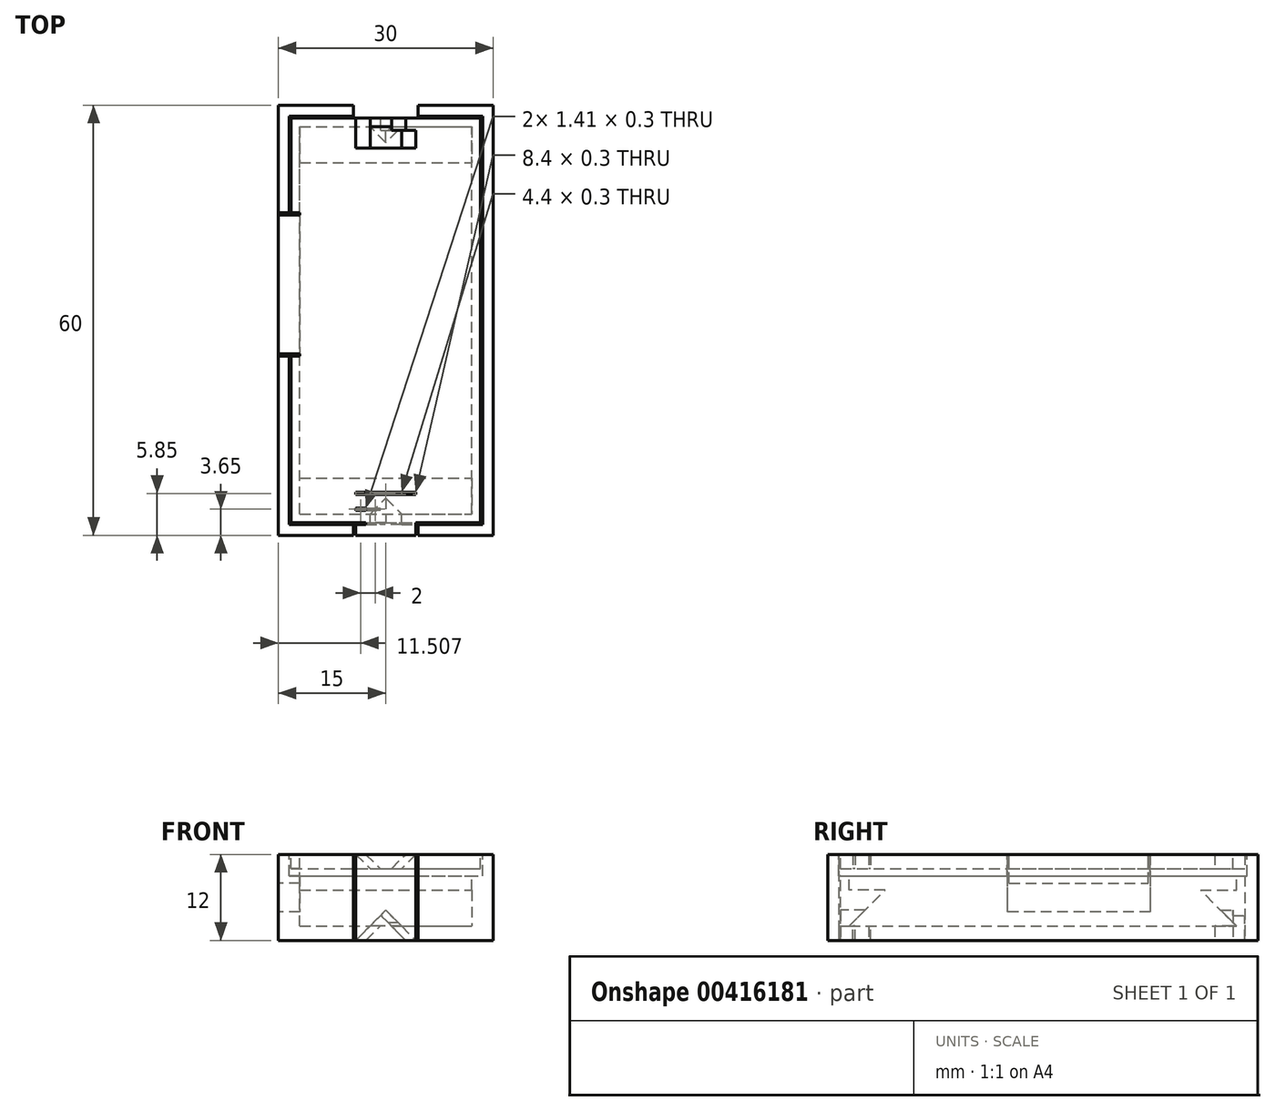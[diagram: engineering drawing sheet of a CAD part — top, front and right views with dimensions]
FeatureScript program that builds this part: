
annotation { "Feature Type Name" : "Feature", "Feature Type Description" : "" }
export const myFeature = defineFeature(function(context is Context, id is Id, definition is map)
    precondition{}
    {
        {
            var Q0;
            Q0=qCreatedBy(makeId("Top.planeOp"),FACE);
            var sketch = newSketch(context, id + "F0", { "sketchPlane" : qUnion([Q0])});
            skLineSegment(sketch, "E0.bottom", {"start": v(0, 0) * mm, "end": v(30, 0) * mm});
            skLineSegment(sketch, "E0.top", {"start": v(0, 60) * mm, "end": v(30, 60) * mm});
            skLineSegment(sketch, "E0.left", {"start": v(0, 0) * mm, "end": v(0, 60) * mm});
            skLineSegment(sketch, "E0.right", {"start": v(30, 0) * mm, "end": v(30, 60) * mm});
            skLineSegment(sketch, "E1.0", {"start": v(1.5, 1.5) * mm, "end": v(1.5, 58.5) * mm});
            skLineSegment(sketch, "E1.1", {"start": v(1.5, 1.5) * mm, "end": v(28.5, 1.5) * mm});
            skLineSegment(sketch, "E1.2", {"start": v(28.5, 1.5) * mm, "end": v(28.5, 58.5) * mm});
            skLineSegment(sketch, "E1.3", {"start": v(1.5, 58.5) * mm, "end": v(28.5, 58.5) * mm});
            skLineSegment(sketch, "E2.0", {"start": v(1.8, 1.8) * mm, "end": v(1.8, 58.2) * mm});
            skLineSegment(sketch, "E2.1", {"start": v(1.8, 1.8) * mm, "end": v(28.2, 1.8) * mm});
            skLineSegment(sketch, "E2.2", {"start": v(28.2, 1.8) * mm, "end": v(28.2, 58.2) * mm});
            skLineSegment(sketch, "E2.3", {"start": v(1.8, 58.2) * mm, "end": v(28.2, 58.2) * mm});
            skLineSegment(sketch, "E3.0", {"start": v(3, 3) * mm, "end": v(3, 57) * mm});
            skLineSegment(sketch, "E3.1", {"start": v(3, 3) * mm, "end": v(27, 3) * mm});
            skLineSegment(sketch, "E3.2", {"start": v(27, 3) * mm, "end": v(27, 57) * mm});
            skLineSegment(sketch, "E3.3", {"start": v(3, 57) * mm, "end": v(27, 57) * mm});
            skSolve(sketch);
        }
        {
            var Q0;
            Q0=makeQuery(id+"F0.imprint","IMPRINT",FACE,{"disambiguationData":[TD([[makeQuery(id+"F0.imprint","IMPRINT",EDGE,{"derivedFrom":sQuery(id+"F0.wireOp",EDGE,"E0.bottom")}),1.0]])]});
            var Q1;
            Q1=makeQuery(id+"F0.imprint","IMPRINT",FACE,{"disambiguationData":[TD([[makeQuery(id+"F0.imprint","IMPRINT",EDGE,{"derivedFrom":sQuery(id+"F0.wireOp",EDGE,"E1.0")}),-1.0]])]});
            var Q2;
            Q2=makeQuery(id+"F0.imprint","IMPRINT",FACE,{"disambiguationData":[TD([[makeQuery(id+"F0.imprint","IMPRINT",EDGE,{"derivedFrom":sQuery(id+"F0.wireOp",EDGE,"E2.0")}),-1.0]])]});
            extrude(context, id + "F1", {"entities" : qUnion([Q0, Q1, Q2]), "oppositeDirection" : true, "depth" : 10 * mm, "offsetDistance" : 25 * mm});
        }
        {
            var Q0;
            Q0=makeQuery(id+"F0.imprint","IMPRINT",FACE,{"disambiguationData":[TD([[makeQuery(id+"F0.imprint","IMPRINT",EDGE,{"derivedFrom":sQuery(id+"F0.wireOp",EDGE,"E2.0")}),-1.0]])]});
            var Q1;
            Q1=makeQuery(id+"F0.imprint","IMPRINT",FACE,{"disambiguationData":[TD([[makeQuery(id+"F0.imprint","IMPRINT",EDGE,{"derivedFrom":sQuery(id+"F0.wireOp",EDGE,"E1.0")}),-1.0]])]});
            extrude(context, id + "F2", {"entities" : qUnion([Q0, Q1]), "operationType" : NewBodyOperationType.REMOVE, "oppositeDirection" : true, "depth" : 3 * mm, "offsetDistance" : 25 * mm});
        }
        {
            var Q0;
            Q0=makeQuery(id+"F1.opExtrude","CAP_FACE",FACE,{"disambiguationData":[OSD([sQuery(id+"F0.wireOp",EDGE,"E0.bottom"),sQuery(id+"F0.wireOp",EDGE,"E0.top"),sQuery(id+"F0.wireOp",EDGE,"E0.left"),sQuery(id+"F0.wireOp",EDGE,"E0.right"),sQuery(id+"F0.wireOp",EDGE,"E3.0"),sQuery(id+"F0.wireOp",EDGE,"E3.1"),sQuery(id+"F0.wireOp",EDGE,"E3.2"),sQuery(id+"F0.wireOp",EDGE,"E3.3")])],"isStart":false});
            var sketch = newSketch(context, id + "F3", { "sketchPlane" : qUnion([Q0])});
            skLineSegment(sketch, "E4.0", {"start": v(0, 0) * mm, "end": v(30, 0) * mm});
            skLineSegment(sketch, "E5.0", {"start": v(30, 0) * mm, "end": v(30, -60) * mm});
            skLineSegment(sketch, "E6.0", {"start": v(0, 0) * mm, "end": v(0, -60) * mm});
            skLineSegment(sketch, "E7.0", {"start": v(0, -60) * mm, "end": v(30, -60) * mm});
            skSolve(sketch);
        }
        {
            var Q0;
            Q0 = qSketchRegion(id + "F3", true);
            extrude(context, id + "F4", {"entities" : qUnion([Q0]), "operationType" : NewBodyOperationType.ADD, "depth" : 2 * mm, "offsetDistance" : 25 * mm});
        }
        {
            var Q0;
            Q0=makeQuery(id+"F1.opExtrude","SWEPT_FACE",FACE,{"disambiguationData":[OSD([sQuery(id+"F0.wireOp",EDGE,"E3.2")])]});
            var sketch = newSketch(context, id + "F5", { "sketchPlane" : qUnion([Q0])});
            skLineSegment(sketch, "E8", {"start": v(-3, -10) * mm, "end": v(-3, -5) * mm});
            skLineSegment(sketch, "E9", {"start": v(-3, -5) * mm, "end": v(-8, -5) * mm});
            skLineSegment(sketch, "E10", {"start": v(-8, -5) * mm, "end": v(-3, -10) * mm});
            skLineSegment(sketch, "E11", {"start": v(-57, -10) * mm, "end": v(-57, -5) * mm});
            skPoint(sketch, "E11.endSnap0", {"position": v(-5.5, -5) * mm});
            skLineSegment(sketch, "E12", {"start": v(-57, -5) * mm, "end": v(-52, -5) * mm});
            skLineSegment(sketch, "E13", {"start": v(-52, -5) * mm, "end": v(-57, -10) * mm});
            skSolve(sketch);
        }
        {
            var Q0;
            Q0 = qSketchRegion(id + "F5", true);
            var Q1;
            Q1=makeQuery(id+"F1.opExtrude","SWEPT_FACE",FACE,{"disambiguationData":[OSD([sQuery(id+"F0.wireOp",EDGE,"E3.0")])]});
            extrude(context, id + "F6", {"entities" : qUnion([Q0]), "operationType" : NewBodyOperationType.ADD, "endBound" : BoundingType.UP_TO_SURFACE, "depth" : 25 * mm, "endBoundEntityFace" : qUnion([Q1]), "offsetDistance" : 25 * mm});
        }
        {
            var Q0;
            Q0=makeQuery(id+"F0.imprint","IMPRINT",FACE,{"disambiguationData":[TD([[makeQuery(id+"F0.imprint","IMPRINT",EDGE,{"derivedFrom":sQuery(id+"F0.wireOp",EDGE,"E2.0")}),-1.0]])]});
            var Q1;
            Q1=makeQuery(id+"F0.imprint","IMPRINT",FACE,{"disambiguationData":[TD([[makeQuery(id+"F0.imprint","IMPRINT",EDGE,{"derivedFrom":sQuery(id+"F0.wireOp",EDGE,"E3.0")}),-1.0]])]});
            extrude(context, id + "F7", {"entities" : qUnion([Q0, Q1]), "oppositeDirection" : true, "depth" : 2 * mm, "offsetDistance" : 25 * mm});
        }
        {
            var Q0;
            Q0=makeQuery(id+"F7.opExtrude","CAP_EDGE",EDGE,{"disambiguationData":[OSD([sQuery(id+"F0.wireOp",EDGE,"E2.1")])],"isStart":false});
            cPlane(context, id + "F8", {"entities" : qUnion([Q0]), "cplaneType" : CPlaneType.MID_PLANE, "offset" : 25 * mm, "width" : 150 * mm, "height" : 150 * mm});
        }
        {
            var Q0;
            Q0=makeQuery(id+"F4.boolean.opBoolean","MERGE",FACE,{"derivedFrom":[makeQuery(id+"F1.opExtrude","SWEPT_FACE",FACE,{"disambiguationData":[OSD([sQuery(id+"F0.wireOp",EDGE,"E0.bottom")])]}),makeQuery(id+"F4.opExtrude","SWEPT_FACE",FACE,{"disambiguationData":[OSD([sQuery(id+"F3.wireOp",EDGE,"E4.0")])]})]});
            var sketch = newSketch(context, id + "F9", { "sketchPlane" : qUnion([Q0])});
            skLineSegment(sketch, "E14", {"start": v(10.5, 0) * mm, "end": v(10.5, -12) * mm});
            skLineSegment(sketch, "E15", {"start": v(19.5, 0) * mm, "end": v(19.5, -12) * mm});
            skLineSegment(sketch, "E16", {"start": v(10.8, 0) * mm, "end": v(12.8, -2) * mm});
            skLineSegment(sketch, "E17", {"start": v(19.2, 0) * mm, "end": v(17.2, -2) * mm});
            skLineSegment(sketch, "E18", {"start": v(12.21, 0) * mm, "end": v(14.21, -2) * mm});
            skLineSegment(sketch, "E19", {"start": v(12.8, -2) * mm, "end": v(17.2, -2) * mm});
            skLineSegment(sketch, "E20", {"start": v(10.8, 0) * mm, "end": v(19.2, 0) * mm});
            skLineSegment(sketch, "E21", {"start": v(10.8, 0) * mm, "end": v(10.8, -12) * mm, "construction": true});
            skLineSegment(sketch, "E22", {"start": v(19.2, 0) * mm, "end": v(19.2, -12) * mm, "construction": true});
            skLineSegment(sketch, "E23", {"start": v(10.8, -12) * mm, "end": v(15, -7.8) * mm});
            skLineSegment(sketch, "E24", {"start": v(15, -7.8) * mm, "end": v(19.2, -12) * mm});
            skLineSegment(sketch, "E25", {"start": v(12.21, -12) * mm, "end": v(15.7, -8.5) * mm});
            skSolve(sketch);
        }
        {
            var Q0;
            {var subQ0=sQuery(id+"F9.wireOp",EDGE,"E14");Q0=makeQuery(id+"F9.imprint","IMPRINT",FACE,{"disambiguationData":[TD([[makeQuery(id+"F9.imprint","IMPRINT",EDGE,{"derivedFrom":subQ0}),1.0]])]});}
            var Q1;
            {var subQ0=sQuery(id+"F9.wireOp",EDGE,"E16");Q1=makeQuery(id+"F9.imprint","IMPRINT",FACE,{"disambiguationData":[TD([[makeQuery(id+"F9.imprint","IMPRINT",EDGE,{"derivedFrom":subQ0}),1.0]])]});}
            var Q2;
            {var subQ0=sQuery(id+"F9.wireOp",EDGE,"E18");Q2=makeQuery(id+"F9.imprint","IMPRINT",FACE,{"disambiguationData":[TD([[makeQuery(id+"F9.imprint","IMPRINT",EDGE,{"derivedFrom":subQ0}),1.0]])]});}
            var Q3;
            {var subQ0=sQuery(id+"F9.wireOp",EDGE,"E17");Q3=makeQuery(id+"F9.imprint","IMPRINT",FACE,{"disambiguationData":[TD([[makeQuery(id+"F9.imprint","IMPRINT",EDGE,{"derivedFrom":subQ0}),-1.0]])]});}
            var Q4;
            {var subQ0=sQuery(id+"F9.wireOp",EDGE,"E25");Q4=makeQuery(id+"F9.imprint","IMPRINT",FACE,{"disambiguationData":[TD([[makeQuery(id+"F9.imprint","IMPRINT",EDGE,{"derivedFrom":subQ0}),-1.0]])]});}
            var Q5;
            {var subQ0=sQuery(id+"F9.wireOp",EDGE,"E23");Q5=makeQuery(id+"F9.imprint","IMPRINT",FACE,{"disambiguationData":[TD([[makeQuery(id+"F9.imprint","IMPRINT",EDGE,{"derivedFrom":subQ0}),-1.0]])]});}
            var Q6;
            Q6=makeQuery(id+"F7.opExtrude","SWEPT_FACE",FACE,{"disambiguationData":[OSD([sQuery(id+"F0.wireOp",EDGE,"E2.1")])]});
            extrude(context, id + "F10", {"entities" : qUnion([Q0, Q1, Q2, Q3, Q4, Q5]), "operationType" : NewBodyOperationType.REMOVE, "endBound" : BoundingType.UP_TO_SURFACE, "oppositeDirection" : true, "depth" : 1.5 * mm, "endBoundEntityFace" : qUnion([Q6]), "offsetDistance" : 25 * mm});
        }
        {
            var Q0;
            {var subQ0=sQuery(id+"F9.wireOp",EDGE,"E18");Q0=makeQuery(id+"F9.imprint","IMPRINT",FACE,{"disambiguationData":[TD([[makeQuery(id+"F9.imprint","IMPRINT",EDGE,{"derivedFrom":subQ0}),1.0]])]});}
            extrude(context, id + "F11", {"entities" : qUnion([Q0]), "operationType" : NewBodyOperationType.REMOVE, "oppositeDirection" : true, "depth" : 6 * mm, "offsetDistance" : 25 * mm});
        }
        {
            var Q0;
            {var subQ0=sQuery(id+"F9.wireOp",EDGE,"E16");Q0=makeQuery(id+"F9.imprint","IMPRINT",FACE,{"disambiguationData":[TD([[makeQuery(id+"F9.imprint","IMPRINT",EDGE,{"derivedFrom":subQ0}),1.0]])]});}
            extrude(context, id + "F12", {"entities" : qUnion([Q0]), "operationType" : NewBodyOperationType.REMOVE, "oppositeDirection" : true, "depth" : 6 * mm, "offsetDistance" : 25 * mm, "hasSecondDirection" : true, "secondDirectionOppositeDirection" : true, "secondDirectionDepth" : 3.5 * mm});
        }
        {
            var Q0;
            Q0=makeQuery(id+"F4.boolean.opBoolean","MERGE",FACE,{"derivedFrom":[makeQuery(id+"F1.opExtrude","SWEPT_FACE",FACE,{"disambiguationData":[OSD([sQuery(id+"F0.wireOp",EDGE,"E0.top")])]}),makeQuery(id+"F4.opExtrude","SWEPT_FACE",FACE,{"disambiguationData":[OSD([sQuery(id+"F3.wireOp",EDGE,"E7.0")])]})]});
            var sketch = newSketch(context, id + "F13", { "sketchPlane" : qUnion([Q0])});
            skLineSegment(sketch, "E26.0", {"start": v(-19.5, 0) * mm, "end": v(-19.5, -12) * mm});
            skLineSegment(sketch, "E27.0", {"start": v(-10.5, 0) * mm, "end": v(-10.5, -12) * mm});
            skLineSegment(sketch, "E28.0", {"start": v(-10.8, 0) * mm, "end": v(-12.8, -2) * mm});
            skLineSegment(sketch, "E29.0", {"start": v(-10.8, 0) * mm, "end": v(-19.2, 0) * mm});
            skLineSegment(sketch, "E30.0", {"start": v(-12.8, -2) * mm, "end": v(-17.2, -2) * mm});
            skLineSegment(sketch, "E31.0", {"start": v(-19.2, 0) * mm, "end": v(-17.2, -2) * mm});
            skLineSegment(sketch, "E32", {"start": v(-15.79, -2) * mm, "end": v(-17.79, 0) * mm});
            skLineSegment(sketch, "E33.0", {"start": v(-10.8, -12) * mm, "end": v(-15, -7.8) * mm});
            skLineSegment(sketch, "E33.1", {"start": v(-15, -7.8) * mm, "end": v(-19.2, -12) * mm});
            skLineSegment(sketch, "E34", {"start": v(-14.3, -8.5) * mm, "end": v(-17.79, -12) * mm});
            skSolve(sketch);
        }
        {
            var Q0;
            {var subQ1=sQuery(id+"F13.wireOp",EDGE,"E26.0");Q0=makeQuery(id+"F13.imprint","IMPRINT",FACE,{"disambiguationData":[TD([[makeQuery(id+"F13.imprint","IMPRINT",EDGE,{"derivedFrom":subQ1}),1.0]])]});}
            var Q1;
            {var subQ0=sQuery(id+"F13.wireOp",EDGE,"E31.0");Q1=makeQuery(id+"F13.imprint","IMPRINT",FACE,{"disambiguationData":[TD([[makeQuery(id+"F13.imprint","IMPRINT",EDGE,{"derivedFrom":subQ0}),1.0]])]});}
            var Q2;
            {var subQ0=sQuery(id+"F13.wireOp",EDGE,"E28.0");Q2=makeQuery(id+"F13.imprint","IMPRINT",FACE,{"disambiguationData":[TD([[makeQuery(id+"F13.imprint","IMPRINT",EDGE,{"derivedFrom":subQ0}),-1.0]])]});}
            var Q3;
            {var subQ3=sQuery(id+"F13.wireOp",EDGE,"E34");Q3=makeQuery(id+"F13.imprint","IMPRINT",FACE,{"disambiguationData":[TD([[makeQuery(id+"F13.imprint","IMPRINT",EDGE,{"derivedFrom":subQ3}),1.0]])]});}
            var Q4;
            {var subQ0=sQuery(id+"F13.wireOp",EDGE,"E33.1");Q4=makeQuery(id+"F13.imprint","IMPRINT",FACE,{"disambiguationData":[TD([[makeQuery(id+"F13.imprint","IMPRINT",EDGE,{"derivedFrom":subQ0}),1.0]])]});}
            var Q5;
            Q5=makeQuery(id+"F7.opExtrude","SWEPT_FACE",FACE,{"disambiguationData":[OSD([sQuery(id+"F0.wireOp",EDGE,"E2.3")])]});
            extrude(context, id + "F14", {"entities" : qUnion([Q0, Q1, Q2, Q3, Q4]), "operationType" : NewBodyOperationType.REMOVE, "endBound" : BoundingType.UP_TO_SURFACE, "oppositeDirection" : true, "depth" : 1.3 * mm, "endBoundEntityFace" : qUnion([Q5]), "offsetDistance" : 25 * mm});
        }
        {
            var Q0;
            {var subQ0=sQuery(id+"F13.wireOp",EDGE,"E28.0");Q0=makeQuery(id+"F13.imprint","IMPRINT",FACE,{"disambiguationData":[TD([[makeQuery(id+"F13.imprint","IMPRINT",EDGE,{"derivedFrom":subQ0}),-1.0]])]});}
            extrude(context, id + "F15", {"entities" : qUnion([Q0]), "operationType" : NewBodyOperationType.REMOVE, "oppositeDirection" : true, "depth" : 6 * mm, "offsetDistance" : 25 * mm});
        }
        {
            var Q0;
            {var subQ0=sQuery(id+"F13.wireOp",EDGE,"E31.0");Q0=makeQuery(id+"F13.imprint","IMPRINT",FACE,{"disambiguationData":[TD([[makeQuery(id+"F13.imprint","IMPRINT",EDGE,{"derivedFrom":subQ0}),1.0]])]});}
            extrude(context, id + "F16", {"entities" : qUnion([Q0]), "operationType" : NewBodyOperationType.REMOVE, "oppositeDirection" : true, "depth" : 6 * mm, "offsetDistance" : 25 * mm, "hasSecondDirection" : true, "secondDirectionOppositeDirection" : true, "secondDirectionDepth" : 3.5 * mm});
        }
        {
            var Q0;
            {var subQ0=sQuery(id+"F9.wireOp",EDGE,"E25");Q0=makeQuery(id+"F9.imprint","IMPRINT",FACE,{"disambiguationData":[TD([[makeQuery(id+"F9.imprint","IMPRINT",EDGE,{"derivedFrom":subQ0}),-1.0]])]});}
            extrude(context, id + "F17", {"entities" : qUnion([Q0]), "operationType" : NewBodyOperationType.REMOVE, "oppositeDirection" : true, "depth" : 6 * mm, "offsetDistance" : 25 * mm});
        }
        {
            var Q0;
            {var subQ0=sQuery(id+"F9.wireOp",EDGE,"E23");Q0=makeQuery(id+"F9.imprint","IMPRINT",FACE,{"disambiguationData":[TD([[makeQuery(id+"F9.imprint","IMPRINT",EDGE,{"derivedFrom":subQ0}),-1.0]])]});}
            extrude(context, id + "F18", {"entities" : qUnion([Q0]), "operationType" : NewBodyOperationType.REMOVE, "oppositeDirection" : true, "depth" : 6 * mm, "offsetDistance" : 25 * mm, "hasSecondDirection" : true, "secondDirectionOppositeDirection" : true, "secondDirectionDepth" : 3.5 * mm});
        }
        {
            var Q0;
            {var subQ1=sQuery(id+"F0.wireOp",EDGE,"E0.right");var subQ2=sQuery(id+"F0.wireOp",EDGE,"E0.bottom");var subQ3=sQuery(id+"F3.wireOp",EDGE,"E4.0");Q0=makeQuery(id+"F10.boolean.opBoolean","SPLIT",FACE,{"disambiguationData":[TD([makeQuery(id+"F1.opExtrude","SWEPT_FACE",FACE,{"disambiguationData":[OSD([subQ1])]})])],"derivedFrom":makeQuery(id+"F4.boolean.opBoolean","MERGE",FACE,{"derivedFrom":[makeQuery(id+"F1.opExtrude","SWEPT_FACE",FACE,{"disambiguationData":[OSD([subQ2])]}),makeQuery(id+"F4.opExtrude","SWEPT_FACE",FACE,{"disambiguationData":[OSD([subQ3])]})]})});}
            var sketch = newSketch(context, id + "F19", { "sketchPlane" : qUnion([Q0])});
            skLineSegment(sketch, "E35.bottom", {"start": v(10.8, 0) * mm, "end": v(19.2, 0) * mm});
            skLineSegment(sketch, "E35.top", {"start": v(10.8, -12) * mm, "end": v(19.2, -12) * mm});
            skLineSegment(sketch, "E35.left", {"start": v(10.8, 0) * mm, "end": v(10.8, -12) * mm});
            skLineSegment(sketch, "E35.right", {"start": v(19.2, 0) * mm, "end": v(19.2, -12) * mm});
            skSolve(sketch);
        }
        {
            var Q0;
            Q0=makeQuery(id+"F19.imprint","IMPRINT",FACE,{"disambiguationData":[TD([[makeQuery(id+"F19.imprint","IMPRINT",EDGE,{"derivedFrom":sQuery(id+"F19.wireOp",EDGE,"E35.bottom")}),-1.0]])]});
            extrude(context, id + "F20", {"entities" : qUnion([Q0]), "oppositeDirection" : true, "depth" : 1.5 * mm, "offsetDistance" : 25 * mm});
        }
        {
            var Q0;
            {var subQ0=sQuery(id+"F9.wireOp",EDGE,"E17");Q0=makeQuery(id+"F9.imprint","IMPRINT",FACE,{"disambiguationData":[TD([[makeQuery(id+"F9.imprint","IMPRINT",EDGE,{"derivedFrom":subQ0}),-1.0]])]});}
            var Q1;
            {var subQ0=sQuery(id+"F9.wireOp",EDGE,"E25");Q1=makeQuery(id+"F9.imprint","IMPRINT",FACE,{"disambiguationData":[TD([[makeQuery(id+"F9.imprint","IMPRINT",EDGE,{"derivedFrom":subQ0}),-1.0]])]});}
            extrude(context, id + "F21", {"entities" : qUnion([Q0, Q1]), "operationType" : NewBodyOperationType.ADD, "oppositeDirection" : true, "depth" : 5.7 * mm, "offsetDistance" : 25 * mm});
        }
        {
            var Q0;
            {var subQ0=sQuery(id+"F9.wireOp",EDGE,"E16");Q0=makeQuery(id+"F9.imprint","IMPRINT",FACE,{"disambiguationData":[TD([[makeQuery(id+"F9.imprint","IMPRINT",EDGE,{"derivedFrom":subQ0}),1.0]])]});}
            var Q1;
            {var subQ0=sQuery(id+"F9.wireOp",EDGE,"E23");Q1=makeQuery(id+"F9.imprint","IMPRINT",FACE,{"disambiguationData":[TD([[makeQuery(id+"F9.imprint","IMPRINT",EDGE,{"derivedFrom":subQ0}),-1.0]])]});}
            extrude(context, id + "F22", {"entities" : qUnion([Q0, Q1]), "operationType" : NewBodyOperationType.ADD, "oppositeDirection" : true, "depth" : 5.7 * mm, "offsetDistance" : 25 * mm, "hasSecondDirection" : true, "secondDirectionOppositeDirection" : true, "secondDirectionDepth" : 3.8 * mm});
        }
        {
            var Q0;
            {var subQ3=sQuery(id+"F13.wireOp",EDGE,"E34");Q0=makeQuery(id+"F13.imprint","IMPRINT",FACE,{"disambiguationData":[TD([[makeQuery(id+"F13.imprint","IMPRINT",EDGE,{"derivedFrom":subQ3}),1.0]])]});}
            extrude(context, id + "F23", {"entities" : qUnion([Q0]), "operationType" : NewBodyOperationType.REMOVE, "oppositeDirection" : true, "depth" : 6 * mm, "offsetDistance" : 25 * mm});
        }
        {
            var Q0;
            {var subQ0=sQuery(id+"F13.wireOp",EDGE,"E33.1");Q0=makeQuery(id+"F13.imprint","IMPRINT",FACE,{"disambiguationData":[TD([[makeQuery(id+"F13.imprint","IMPRINT",EDGE,{"derivedFrom":subQ0}),1.0]])]});}
            extrude(context, id + "F24", {"entities" : qUnion([Q0]), "operationType" : NewBodyOperationType.REMOVE, "oppositeDirection" : true, "depth" : 6 * mm, "offsetDistance" : 25 * mm, "hasSecondDirection" : true, "secondDirectionOppositeDirection" : true, "secondDirectionDepth" : 3.5 * mm});
        }
        {
            var Q0;
            Q0=makeQuery(id+"F4.boolean.opBoolean","MERGE",FACE,{"derivedFrom":[makeQuery(id+"F1.opExtrude","SWEPT_FACE",FACE,{"disambiguationData":[OSD([sQuery(id+"F0.wireOp",EDGE,"E0.left")])]}),makeQuery(id+"F4.opExtrude","SWEPT_FACE",FACE,{"disambiguationData":[OSD([sQuery(id+"F3.wireOp",EDGE,"E6.0")])]})]});
            var sketch = newSketch(context, id + "F25", { "sketchPlane" : qUnion([Q0])});
            skLineSegment(sketch, "E36.bottom", {"start": v(-45, 0) * mm, "end": v(-25, 0) * mm});
            skLineSegment(sketch, "E36.top", {"start": v(-45, -8) * mm, "end": v(-25, -8) * mm});
            skLineSegment(sketch, "E36.left", {"start": v(-45, 0) * mm, "end": v(-45, -8) * mm});
            skLineSegment(sketch, "E36.right", {"start": v(-25, 0) * mm, "end": v(-25, -8) * mm});
            skSolve(sketch);
        }
        {
            var Q0;
            Q0 = qSketchRegion(id + "F25", true);
            var Q1;
            Q1=makeQuery(id+"F1.opExtrude","SWEPT_FACE",FACE,{"disambiguationData":[OSD([sQuery(id+"F0.wireOp",EDGE,"E3.0")])]});
            extrude(context, id + "F26", {"entities" : qUnion([Q0]), "operationType" : NewBodyOperationType.REMOVE, "endBound" : BoundingType.UP_TO_SURFACE, "oppositeDirection" : true, "depth" : 25 * mm, "endBoundEntityFace" : qUnion([Q1]), "offsetDistance" : 25 * mm});
        }
        {
            var Q0;
            Q0=makeQuery(id+"F7.opExtrude","CAP_FACE",FACE,{"disambiguationData":[OSD([sQuery(id+"F0.wireOp",EDGE,"E2.0"),sQuery(id+"F0.wireOp",EDGE,"E2.1"),sQuery(id+"F0.wireOp",EDGE,"E2.2"),sQuery(id+"F0.wireOp",EDGE,"E2.3")])],"isStart":true});
            var sketch = newSketch(context, id + "F27", { "sketchPlane" : qUnion([Q0])});
            skLineSegment(sketch, "E37.bottom", {"start": v(3, 44.7) * mm, "end": v(0, 44.7) * mm});
            skLineSegment(sketch, "E37.top", {"start": v(3, 25.3) * mm, "end": v(0, 25.3) * mm});
            skLineSegment(sketch, "E37.left", {"start": v(3, 44.7) * mm, "end": v(3, 25.3) * mm});
            skLineSegment(sketch, "E37.right", {"start": v(0, 44.7) * mm, "end": v(0, 25.3) * mm});
            skSolve(sketch);
        }
        {
            var Q0;
            Q0 = qSketchRegion(id + "F27", true);
            extrude(context, id + "F28", {"entities" : qUnion([Q0]), "operationType" : NewBodyOperationType.ADD, "oppositeDirection" : true, "depth" : 4 * mm, "offsetDistance" : 25 * mm});
        }
        {
            var Q0;
            {var subQ0=sQuery(id+"F9.wireOp",EDGE,"E25");var subQ1=sQuery(id+"F9.wireOp",EDGE,"E24");var subQ2=sQuery(id+"F3.wireOp",EDGE,"E4.0");Q0=makeQuery(id+"F22.boolean.opBoolean","MERGE",FACE,{"derivedFrom":[makeQuery(id+"F21.opExtrude","CAP_FACE",FACE,{"disambiguationData":[OSD([subQ2,subQ1,subQ0])],"isStart":false}),makeQuery(id+"F22.opExtrude","CAP_FACE",FACE,{"disambiguationData":[OSD([subQ2,sQuery(id+"F9.wireOp",EDGE,"E23"),subQ1,subQ0])],"isStart":false})]});}
            var sketch = newSketch(context, id + "F29", { "sketchPlane" : qUnion([Q0])});
            skLineSegment(sketch, "E38.0", {"start": v(-15, -7.8) * mm, "end": v(-17.2, -10) * mm});
            skLineSegment(sketch, "E39.0", {"start": v(-12.8, -10) * mm, "end": v(-15, -7.8) * mm});
            skLineSegment(sketch, "E40", {"start": v(-17.2, -10) * mm, "end": v(-12.8, -10) * mm});
            skPoint(sketch, "E41.orphan", {"position": v(-19.2, -12) * mm});
            skPoint(sketch, "E42.orphan", {"position": v(-10.8, -12) * mm});
            skSolve(sketch);
        }
        {
            var Q0;
            Q0 = qSketchRegion(id + "F29", true);
            var Q1;
            Q1=makeQuery(id+"F20.opExtrude","CAP_FACE",FACE,{"disambiguationData":[OSD([sQuery(id+"F19.wireOp",EDGE,"E35.bottom"),sQuery(id+"F19.wireOp",EDGE,"E35.top"),sQuery(id+"F19.wireOp",EDGE,"E35.left"),sQuery(id+"F19.wireOp",EDGE,"E35.right")])],"isStart":false});
            extrude(context, id + "F30", {"entities" : qUnion([Q0]), "operationType" : NewBodyOperationType.REMOVE, "endBound" : BoundingType.UP_TO_SURFACE, "oppositeDirection" : true, "depth" : 25 * mm, "endBoundEntityFace" : qUnion([Q1]), "offsetDistance" : 25 * mm});
        }
    });
